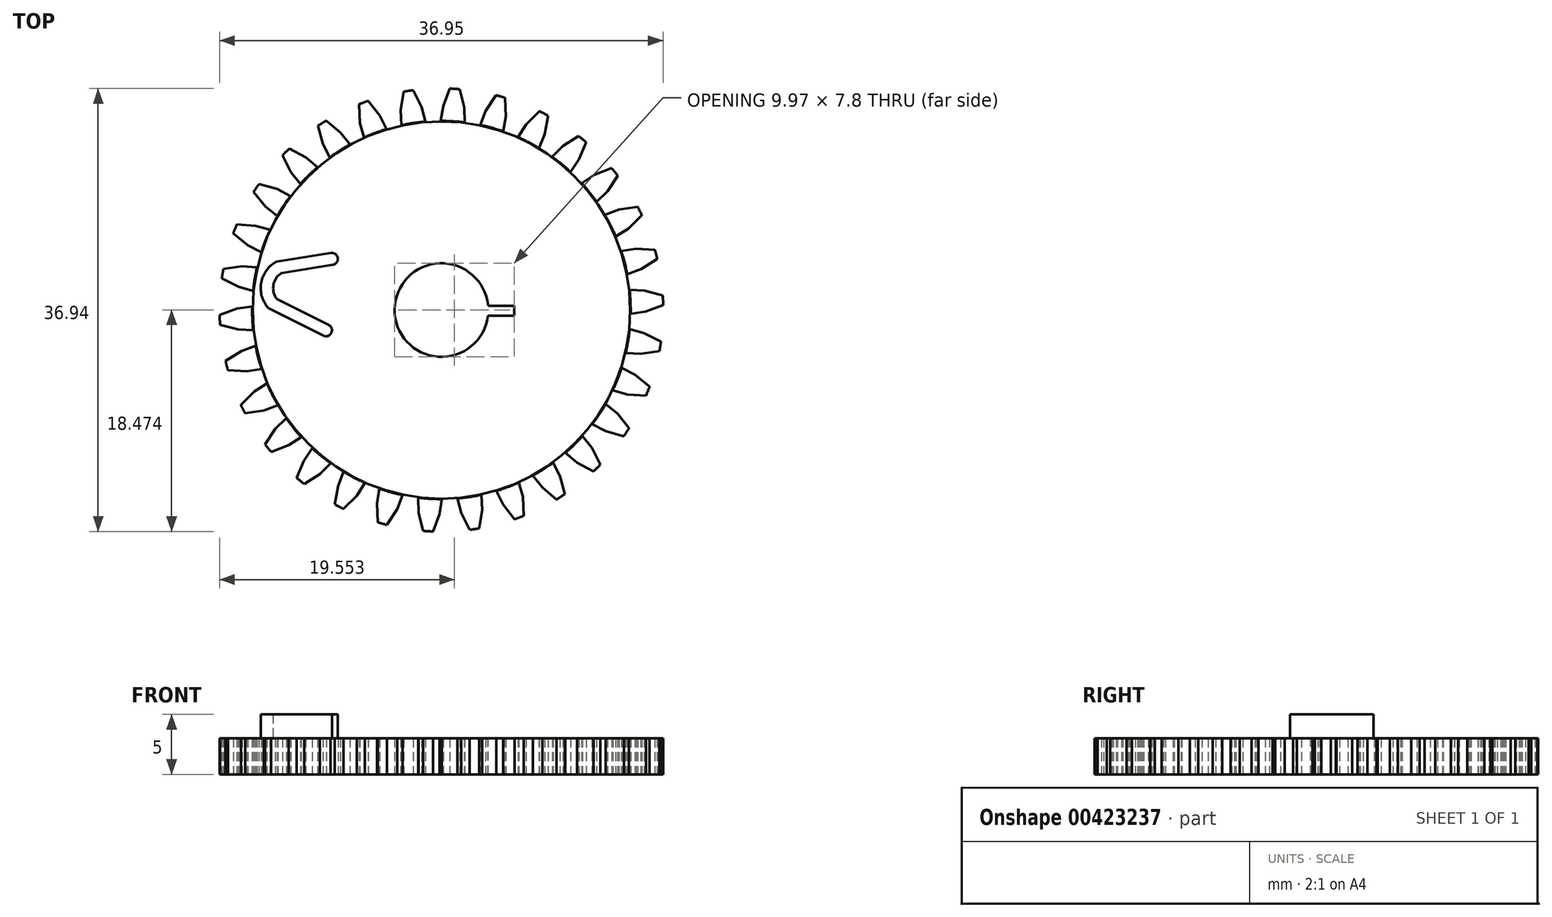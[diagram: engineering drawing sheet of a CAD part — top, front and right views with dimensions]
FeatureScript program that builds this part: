
annotation { "Feature Type Name" : "Feature", "Feature Type Description" : "" }
export const myFeature = defineFeature(function(context is Context, id is Id, definition is map)
    precondition{}
    {
        {
            var Q0;
            Q0=qCreatedBy(makeId("Top.planeOp"),FACE);
            var sketch = newSketch(context, id + "F0", { "sketchPlane" : qUnion([Q0])});
            skLineSegment(sketch, "E0", {"start": v(2.7, 43.64) * mm, "end": v(12.7, 43.64) * mm});
            skSolve(sketch);
        }
        {
            var Q0;
            Q0=qCreatedBy(makeId("Top.planeOp"),FACE);
            var sketch = newSketch(context, id + "F1", { "sketchPlane" : qUnion([Q0])});
            skLineSegment(sketch, "E1.0", {"start": v(2.7, 43.64) * mm, "end": v(12.7, 43.64) * mm});
            skLineSegment(sketch, "E2.top", {"start": v(2.7, -76.36) * mm, "end": v(12.7, -76.36) * mm});
            skLineSegment(sketch, "E2.left", {"start": v(2.7, 43.64) * mm, "end": v(2.7, -76.36) * mm});
            skLineSegment(sketch, "E2.right", {"start": v(12.7, 43.64) * mm, "end": v(12.7, -76.36) * mm});
            skLineSegment(sketch, "E3", {"start": v(2.7, 25.61) * mm, "end": v(12.7, 25.61) * mm, "construction": true});
            skLineSegment(sketch, "E4", {"start": v(-0.54, 23.36) * mm, "end": v(2.7, 23.36) * mm, "construction": true});
            skLineSegment(sketch, "E5.trimOffspring", {"start": v(12.7, 23.36) * mm, "end": v(15.96, 23.36) * mm, "construction": true});
            skSolve(sketch);
        }
        {
            var Q0;
            Q0=qCreatedBy(makeId("Top.planeOp"),FACE);
            var sketch = newSketch(context, id + "F2", { "sketchPlane" : qUnion([Q0])});
            skCircle(sketch, "E6", {"center": v(-27.08, -9.47) * mm, "radius": 3.83 * mm, "construction": true});
            skPoint(sketch, "E6.first.point", {"position": v(-30.8, -8.51) * mm});
            skPoint(sketch, "E6.second.point", {"position": v(-24.15, -7) * mm});
            skPoint(sketch, "E6.third.point", {"position": v(-26, -13.15) * mm});
            skPoint(sketch, "E7.0", {"position": v(7.7, 43.64) * mm});
            skLineSegment(sketch, "E8", {"start": v(7.7, -76.2) * mm, "end": v(7.7, 35.56) * mm, "construction": true});
            skLineSegment(sketch, "E9", {"start": v(85.63, -9.47) * mm, "end": v(-27.08, -9.47) * mm, "construction": true});
            skCircle(sketch, "E10.MirrorC", {"center": v(42.47, -9.47) * mm, "radius": 3.83 * mm, "construction": true});
            skCircle(sketch, "E11", {"center": v(-27.08, -9.47) * mm, "radius": 15.77 * mm, "construction": true});
            skCircle(sketch, "E12.MirrorC", {"center": v(42.47, -9.47) * mm, "radius": 15.77 * mm, "construction": true});
            skCircle(sketch, "E13.MirrorC", {"center": v(7.7, -9.47) * mm, "radius": 3.83 * mm, "construction": true});
            skCircle(sketch, "E14.MirrorC", {"center": v(7.7, -9.47) * mm, "radius": 15.77 * mm, "construction": true});
            skSolve(sketch);
        }
        {
            var Q0;
            Q0=qCreatedBy(makeId("Top.planeOp"),FACE);
            var sketch = newSketch(context, id + "F3", { "sketchPlane" : qUnion([Q0])});
            skPoint(sketch, "E15.0", {"position": v(42.47, -9.47) * mm});
            skCircle(sketch, "E16.0", {"center": v(42.47, -9.47) * mm, "radius": 15.77 * mm});
            skCircle(sketch, "E17.0", {"center": v(42.47, -9.47) * mm, "radius": 3.83 * mm});
            skLineSegment(sketch, "E18.0", {"start": v(7.7, -76.2) * mm, "end": v(7.7, 35.56) * mm});
            skLineSegment(sketch, "E19.0", {"start": v(85.63, -9.47) * mm, "end": v(-27.08, -9.47) * mm});
            skCircle(sketch, "E20.0", {"center": v(7.7, -9.47) * mm, "radius": 3.83 * mm});
            skCircle(sketch, "E21.0", {"center": v(-27.08, -9.47) * mm, "radius": 3.83 * mm});
            skCircle(sketch, "E22", {"center": v(42.47, -9.47) * mm, "radius": 15.73 * mm});
            skCircle(sketch, "E23", {"center": v(42.47, -9.47) * mm, "radius": 3.9 * mm});
            skArc(sketch, "E24", {"start": v(38.49, 5.79) * mm, "mid": v(40.14, 6.13) * mm, "end": v(41.82, 6.29) * mm});
            skLineSegment(sketch, "E25", {"start": v(39.15, 5.94) * mm, "end": v(39.08, 7.2) * mm});
            skLineSegment(sketch, "E26", {"start": v(42.47, -9.47) * mm, "end": v(40.14, 6.09) * mm, "construction": true});
            skPoint(sketch, "E26.endSnap0", {"position": v(40.14, 6.13) * mm});
            skLineSegment(sketch, "E27", {"start": v(40.14, 6.09) * mm, "end": v(39.58, 9.82) * mm, "construction": true});
            skLineSegment(sketch, "E28", {"start": v(39.08, 7.2) * mm, "end": v(39.33, 8.74) * mm});
            skLineSegment(sketch, "E29.MirrorCS", {"start": v(40.82, 7.46) * mm, "end": v(40.13, 8.86) * mm});
            skLineSegment(sketch, "E30.MirrorCS", {"start": v(41.13, 6.24) * mm, "end": v(40.82, 7.46) * mm});
            skArc(sketch, "E31.trimOffspring", {"start": v(40.13, 8.86) * mm, "mid": v(39.73, 8.8) * mm, "end": v(39.33, 8.74) * mm});
            skSolve(sketch);
        }
        {
            var Q0;
            {var subQ0=sQuery(id+"F3.wireOp",EDGE,"E22");var subQ1=sQuery(id+"F3.wireOp",EDGE,"E19.0");var subQ2=makeQuery(id+"F3.imprint","INTERSECT",VERTEX,{"disambiguationData":[OD(0.0)],"derivedFrom":[subQ1,subQ0]});Q0=makeQuery(id+"F3.imprint","IMPRINT",FACE,{"disambiguationData":[TD([[makeQuery(id+"F3.imprint","IMPRINT",EDGE,{"disambiguationData":[TD([[subQ2,-1.0]])],"derivedFrom":subQ1}),-1.0]])]});}
            var Q1;
            {var subQ0=sQuery(id+"F3.wireOp",EDGE,"E22");var subQ1=sQuery(id+"F3.wireOp",EDGE,"E19.0");var subQ2=makeQuery(id+"F3.imprint","INTERSECT",VERTEX,{"disambiguationData":[OD(0.0)],"derivedFrom":[subQ1,subQ0]});Q1=makeQuery(id+"F3.imprint","IMPRINT",FACE,{"disambiguationData":[TD([[makeQuery(id+"F3.imprint","IMPRINT",EDGE,{"disambiguationData":[TD([[subQ2,-1.0]])],"derivedFrom":subQ1}),1.0]])]});}
            extrude(context, id + "F4", {"entities" : qUnion([Q0, Q1]), "depth" : 3 * mm});
        }
        {
            var Q0;
            Q0=qSketchRegion(id+"F2",true);
            var Q1;
            {var subQ0=sQuery(id+"F3.wireOp",EDGE,"E25");Q1=makeQuery(id+"F3.imprint","IMPRINT",FACE,{"disambiguationData":[TD([[makeQuery(id+"F3.imprint","IMPRINT",EDGE,{"derivedFrom":subQ0}),-1.0]])]});}
            var Q2;
            Q2=makeQuery(id+"F4.opExtrude","CAP_FACE",FACE,{"disambiguationData":[OSD([sQuery(id+"F3.wireOp",EDGE,"E22"),sQuery(id+"F3.wireOp",EDGE,"E23")])],"isStart":false});
            extrude(context, id + "F5", {"entities" : qUnion([Q0, Q1]), "endBound" : BoundingType.UP_TO_SURFACE, "endBoundEntityFace" : qUnion([Q2]), "depth" : 25 * mm});
        }
        {
            var Q0;
            Q0=makeQuery(id+"F5.opExtrude","SWEPT_BODY",BODY,{"disambiguationData":[OSD([sQuery(id+"F3.wireOp",EDGE,"E16.0"),sQuery(id+"F3.wireOp",EDGE,"E25"),sQuery(id+"F3.wireOp",EDGE,"E28"),sQuery(id+"F3.wireOp",EDGE,"E29.MirrorCS"),sQuery(id+"F3.wireOp",EDGE,"E30.MirrorCS"),sQuery(id+"F3.wireOp",EDGE,"E31.trimOffspring")])]});
            var Q1;
            Q1=sQuery(id+"F3.wireOp",EDGE,"E22");
            circularPattern(context, id + "F6", {"entities" : qUnion([Q0]), "axis" : qUnion([Q1]), "angle" : 360 * degree, "instanceCount" : 30, "equalSpace" : true, "isCentered" : true});
        }
        {
            var Q0;
            Q0=qCreatedBy(makeId("Top.planeOp"),FACE);
            var sketch = newSketch(context, id + "F7", { "sketchPlane" : qUnion([Q0])});
            skLineSegment(sketch, "E32", {"start": v(33.27, -4.72) * mm, "end": v(28.74, -5.44) * mm});
            skArc(sketch, "E33", {"start": v(28.68, -5.46) * mm, "mid": v(27.46, -7.2) * mm, "end": v(28, -9.25) * mm});
            skLineSegment(sketch, "E34", {"start": v(28.05, -9.3) * mm, "end": v(32.63, -11.6) * mm});
            skArc(sketch, "E35.0", {"start": v(29.1, -6.41) * mm, "mid": v(28.48, -7.36) * mm, "end": v(28.7, -8.48) * mm});
            skLineSegment(sketch, "E36.0", {"start": v(28.77, -8.54) * mm, "end": v(33.08, -10.71) * mm});
            skArc(sketch, "E37.filletArc", {"start": v(28.7, -8.48) * mm, "mid": v(28.74, -8.51) * mm, "end": v(28.77, -8.54) * mm});
            skPoint(sketch, "E38.visualSharp", {"position": v(28.7, -5.45) * mm});
            skArc(sketch, "E38.filletArc", {"start": v(28.74, -5.44) * mm, "mid": v(28.7, -5.45) * mm, "end": v(28.68, -5.46) * mm});
            skPoint(sketch, "E39.visualSharp", {"position": v(28.02, -9.28) * mm});
            skArc(sketch, "E39.filletArc", {"start": v(28, -9.25) * mm, "mid": v(28.02, -9.27) * mm, "end": v(28.05, -9.3) * mm});
            skLineSegment(sketch, "E40.0", {"start": v(33.43, -5.7) * mm, "end": v(29.17, -6.39) * mm});
            skArc(sketch, "E41", {"start": v(33.43, -5.7) * mm, "mid": v(33.84, -5.13) * mm, "end": v(33.27, -4.72) * mm});
            skArc(sketch, "E42", {"start": v(32.63, -11.6) * mm, "mid": v(33.3, -11.38) * mm, "end": v(33.08, -10.71) * mm});
            skArc(sketch, "E43.filletArc", {"start": v(29.17, -6.39) * mm, "mid": v(29.13, -6.4) * mm, "end": v(29.1, -6.41) * mm});
            skPoint(sketch, "E44.0", {"position": v(7.7, -9.47) * mm});
            skPoint(sketch, "E45.0", {"position": v(42.47, -9.47) * mm});
            skSolve(sketch);
        }
        {
            var Q0;
            Q0=qSketchRegion(id+"F7",true);
            extrude(context, id + "F8", {"entities" : qUnion([Q0]), "operationType" : NewBodyOperationType.ADD, "depth" : 5 * mm});
        }
        {
            var Q0;
            Q0=makeQuery(id+"F4.opExtrude","CAP_FACE",FACE,{"disambiguationData":[OSD([sQuery(id+"F3.wireOp",EDGE,"E22"),sQuery(id+"F3.wireOp",EDGE,"E23")])],"isStart":false});
            var sketch = newSketch(context, id + "F9", { "sketchPlane" : qUnion([Q0])});
            skLineSegment(sketch, "E46.bottom", {"start": v(46.35, -9.94) * mm, "end": v(48.54, -9.94) * mm});
            skLineSegment(sketch, "E46.top", {"start": v(46.35, -9.12) * mm, "end": v(48.54, -9.12) * mm});
            skLineSegment(sketch, "E46.left", {"start": v(46.35, -9.94) * mm, "end": v(46.35, -9.12) * mm});
            skLineSegment(sketch, "E46.right", {"start": v(48.54, -9.94) * mm, "end": v(48.54, -9.12) * mm});
            skSolve(sketch);
        }
        {
            var Q0;
            {var subQ0=sQuery(id+"F9.wireOp",EDGE,"E46.bottom");Q0=makeQuery(id+"F9.imprint","IMPRINT",FACE,{"disambiguationData":[TD([[makeQuery(id+"F9.imprint","IMPRINT",EDGE,{"derivedFrom":subQ0}),1.0]])]});}
            extrude(context, id + "F10", {"entities" : qUnion([Q0]), "operationType" : NewBodyOperationType.REMOVE, "oppositeDirection" : true, "depth" : 25 * mm});
        }
    });
